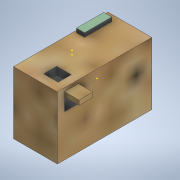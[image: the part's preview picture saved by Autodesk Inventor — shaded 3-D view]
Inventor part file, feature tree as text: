
AUTODESK INVENTOR PART (.ipt)
format: ipt  version: 2021 (Build 250183000, 183)  size: 259,072 bytes
history: native  units: mm
features: sketch x25, extrude x16
ambient origin geometry x8: Origin, YZ Plane, XZ Plane, XY Plane, X Axis, Y Axis, Z Axis, Center Point
bodies: Solid1 (feature_tree)
feature tree (41):
  extrude  "Extrusion1"  Depth=3.0mm TaperAngle=0.0deg
  extrude  "Extrusion2"  Depth=1.5mm TaperAngle=0.0deg
  extrude  "Extrusion3"  Depth=32.5mm TaperAngle=0.0deg
  extrude  "Extrusion4"  Depth=1.5mm TaperAngle=0.0deg
  extrude  "Extrusion5"  Depth=1.5mm TaperAngle=0.0deg
  extrude  "Extrusion6"  Depth=1.0mm TaperAngle=0.0deg
  extrude  "Extrusion7"  Depth=1.0mm TaperAngle=0.0deg
  sketch  "Sketch8"  dims[d31=7.0mm d32=0.0mm d33=1.5mm d34=0.0mm]
  extrude  "Extrusion9"  Depth=1.5mm TaperAngle=0.0deg
  sketch  "Sketch11"
  extrude  "Extrusion10"  [1 undecoded]
  extrude  "Extrusion11"  [1 undecoded]
  extrude  "Extrusion12"  [1 undecoded]
  extrude  "Extrusion13"  [1 undecoded]
  extrude  "Extrusion15"  [1 undecoded]
  extrude  "Extrusion16"  [1 undecoded]
  sketch  "Sketch20"
  sketch  "Sketch21"
  sketch  "Sketch22"
  extrude  "Extrusion17"  [1 undecoded]
  sketch  "Sketch24"
  sketch  "Sketch25"
  sketch  "Sketch26"
  extrude  "Extrusion18"  [1 undecoded]
  sketch  "Sketch28"
  sketch  "Sketch1"  dims[d0=15.0mm d1=3.0mm d2=0.0mm]
  sketch  "Sketch2"  dims[d3=4.5mm d4=0.0mm d5=1.5mm d6=0.0mm]
  sketch  "Sketch3"  dims[d7=1.5mm d8=0.0mm d9=32.5mm d10=0.0mm]
  sketch  "Sketch4"  dims[d11=1.5mm d12=0.0mm d13=1.5mm d14=0.0mm]
  sketch  "Sketch5"  dims[d17=1.5mm d18=0.0mm d19=1.5mm d20=0.0mm]
  sketch  "Sketch6"  dims[d21=1.0mm d22=0.0mm d23=1.0mm d24=0.0mm]
  sketch  "Sketch7"  dims[d25=1.0mm d26=0.0mm d29=1.0mm d30=0.0mm]
  sketch  "Sketch10"  dims[d35=1.5mm d36=0.0mm]
  sketch  "Sketch12"
  sketch  "Sketch13"
  sketch  "Sketch14"
  sketch  "Sketch15"
  sketch  "Sketch17"
  sketch  "Sketch19"
  sketch  "Sketch23"
  sketch  "Sketch27"
note: 8 required parameter values undecoded (feature->parameter linkage not recoverable at this tier; creation-order binding heuristic only, values carry confidence <= 0.55)
